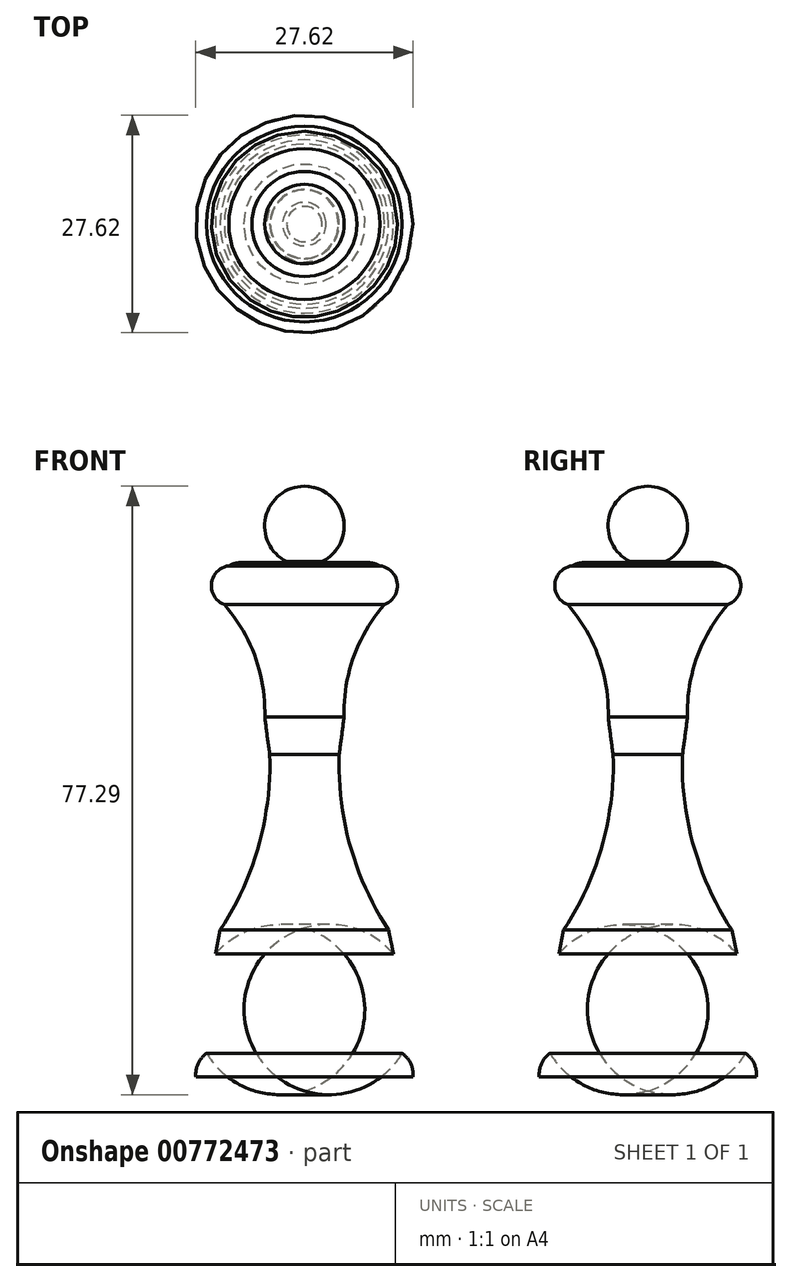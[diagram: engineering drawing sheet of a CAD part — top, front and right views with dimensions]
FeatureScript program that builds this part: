
annotation { "Feature Type Name" : "Feature", "Feature Type Description" : "" }
export const myFeature = defineFeature(function(context is Context, id is Id, definition is map)
    precondition{}
    {
        {
            var Q0;
            Q0=qCreatedBy(makeId("Front.planeOp"),FACE);
            var sketch = newSketch(context, id + "F0", { "sketchPlane" : qUnion([Q0])});
            skLineSegment(sketch, "E0", {"start": v(0, 0) * mm, "end": v(13.8, 0) * mm});
            skArc(sketch, "E1", {"start": v(13.8, 0) * mm, "mid": v(13.5, 1.67) * mm, "end": v(12.42, 2.97) * mm});
            skArc(sketch, "E2", {"start": v(12.42, 2.97) * mm, "mid": v(13.92, 9.47) * mm, "end": v(11.31, 15.6) * mm});
            skArc(sketch, "E3", {"start": v(4.4, 40.93) * mm, "mid": v(5.83, 29.29) * mm, "end": v(10.7, 18.62) * mm});
            skArc(sketch, "E4", {"start": v(10.17, 59.97) * mm, "mid": v(6.25, 53.31) * mm, "end": v(5.03, 45.68) * mm});
            skArc(sketch, "E5", {"start": v(10.17, 59.97) * mm, "mid": v(11.8, 62.66) * mm, "end": v(9.6, 64.9) * mm});
            skLineSegment(sketch, "E6", {"start": v(0, 63.75) * mm, "end": v(0, 0) * mm});
            skLineSegment(sketch, "E7", {"start": v(9.6, 64.9) * mm, "end": v(0, 64.9) * mm});
            skLineSegment(sketch, "E8", {"start": v(0, 63.75) * mm, "end": v(0, 64.9) * mm});
            skArc(sketch, "E9", {"start": v(2.25, 65.42) * mm, "mid": v(4.92, 71.1) * mm, "end": v(0, 75) * mm});
            skLineSegment(sketch, "E10", {"start": v(0, 75) * mm, "end": v(0, 64.9) * mm});
            skLineSegment(sketch, "E11", {"start": v(2.25, 65.42) * mm, "end": v(2.77, 64.9) * mm});
            skArc(sketch, "E12", {"start": v(9.6, 64.9) * mm, "mid": v(8.13, 65.3) * mm, "end": v(6.68, 64.9) * mm});
            skArc(sketch, "E13", {"start": v(6.68, 64.9) * mm, "mid": v(5.5, 65.33) * mm, "end": v(4.32, 64.9) * mm});
            skArc(sketch, "E14", {"start": v(4.32, 64.9) * mm, "mid": v(3.54, 65.25) * mm, "end": v(2.77, 64.9) * mm});
            skPoint(sketch, "E15.endSnap0", {"position": v(6.1, 40.93) * mm});
            skPoint(sketch, "E15.end.orphan", {"position": v(6.1, 28.35) * mm});
            skLineSegment(sketch, "E16", {"start": v(10.7, 18.62) * mm, "end": v(11.31, 15.6) * mm});
            skPoint(sketch, "E17.start.orphan", {"position": v(7.8, 40.93) * mm});
            skPoint(sketch, "E18.end.orphan", {"position": v(7.8, 45.68) * mm});
            skArc(sketch, "E19", {"start": v(4.4, 40.93) * mm, "mid": v(4.74, 43.3) * mm, "end": v(5.03, 45.68) * mm});
            skSolve(sketch);
        }
        {
            var Q0;
            Q0 = qSketchRegion(id + "F0", true);
            var Q1;
            Q1=sQuery(id+"F0.wireOp",EDGE,"E6");
            revolve(context, id + "F1", {"surfaceOperationType" : NewSurfaceOperationType.NEW, "entities" : qUnion([Q0]), "axis" : qUnion([Q1]), "revolveType" : RevolveType.FULL});
        }
    });
